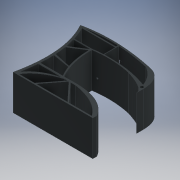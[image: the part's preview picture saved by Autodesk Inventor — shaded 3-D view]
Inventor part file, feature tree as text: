
AUTODESK INVENTOR PART (.ipt)
format: ipt  version: 2018 (Build 220112000, 112)  size: 264,704 bytes
history: native  units: mm
features: extrude x3, sketch x3, plane x2
ambient origin geometry x8: Origin, YZ Plane, XZ Plane, XY Plane, X Axis, Y Axis, Z Axis, Center Point
bodies: Solid1 (feature_tree)
feature tree (8):
  extrude  "Extrusion1"  Depth=30.0mm
  plane  "Work Plane1"
  extrude  "Extrusion2"  Depth=820.0mm TaperAngle=0.0deg
  plane  "Work Plane2"
  extrude  "Extrusion3"  Depth=392.0mm
  sketch  "Sketch1"  dims[d13=400.0mm d25=30.0mm]
  sketch  "Sketch2"  dims[d27=72.0mm d28=820.0mm d29=0.0mm]
  sketch  "Sketch3"  dims[d30=520.0mm d31=392.0mm d32=37.25mm d33=0.0mm d34=40.0mm d35=874.75mm d36=0.0mm]
